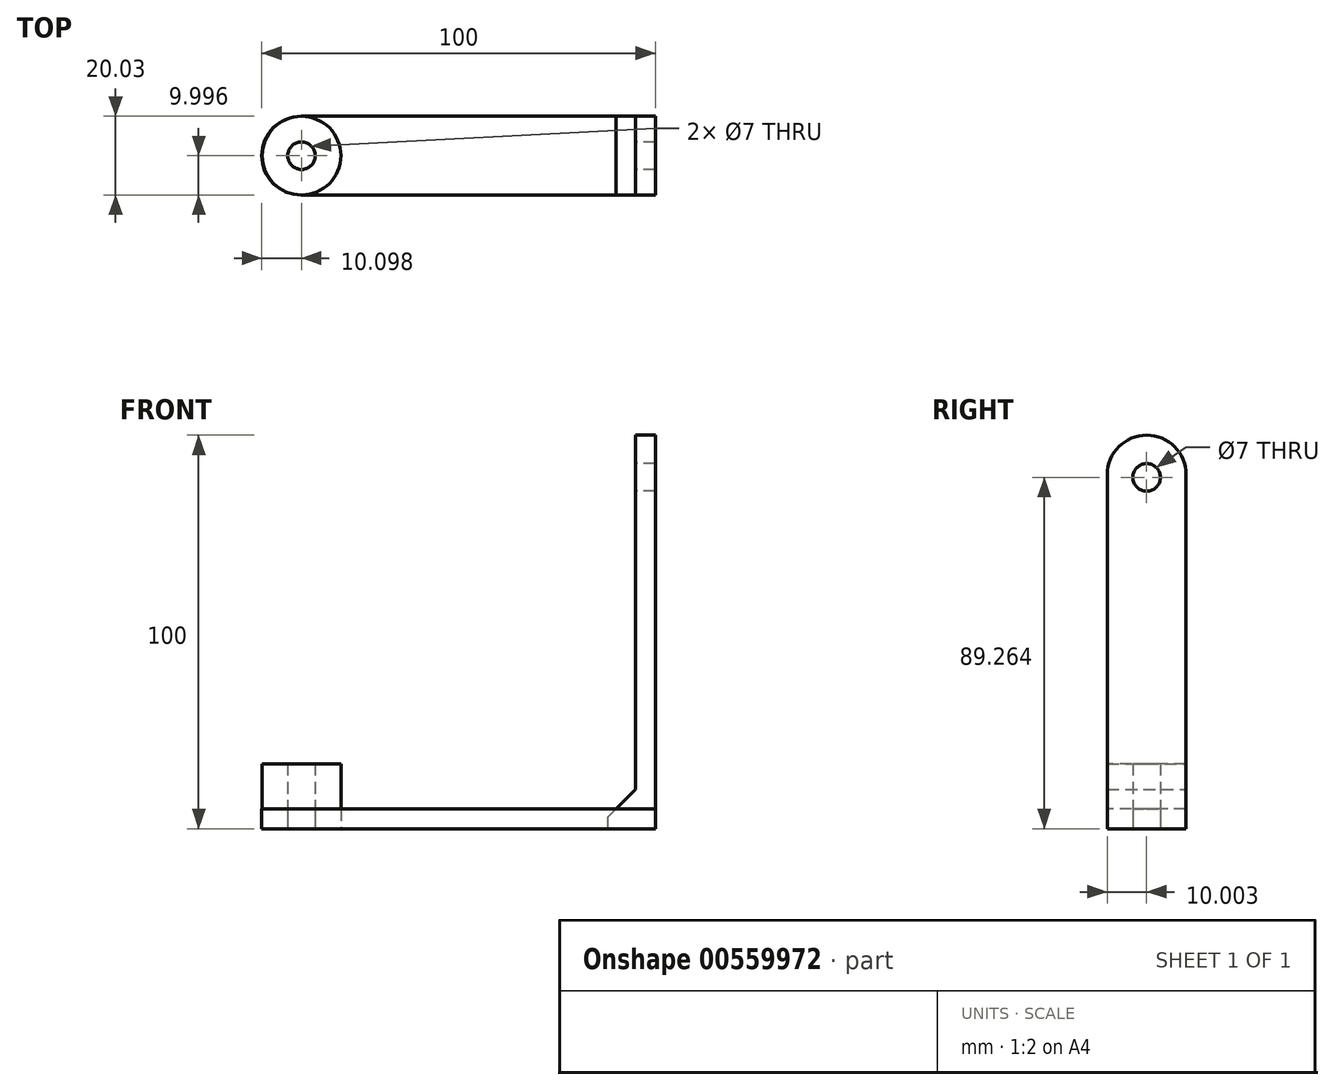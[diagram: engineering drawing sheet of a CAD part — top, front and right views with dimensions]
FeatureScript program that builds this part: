
annotation { "Feature Type Name" : "Feature", "Feature Type Description" : "" }
export const myFeature = defineFeature(function(context is Context, id is Id, definition is map)
    precondition{}
    {
        {
            var Q0;
            Q0=qCreatedBy(makeId("Top.planeOp"),FACE);
            var sketch = newSketch(context, id + "F0", { "sketchPlane" : qUnion([Q0])});
            skLineSegment(sketch, "E0.bottom", {"start": v(-46.2, 30.05) * mm, "end": v(53.8, 30.05) * mm});
            skLineSegment(sketch, "E0.top", {"start": v(-46.2, 10.05) * mm, "end": v(53.8, 10.05) * mm});
            skLineSegment(sketch, "E0.left", {"start": v(-46.2, 30.05) * mm, "end": v(-46.2, 10.05) * mm});
            skLineSegment(sketch, "E0.right", {"start": v(53.8, 30.05) * mm, "end": v(53.8, 10.05) * mm});
            skLineSegment(sketch, "E1", {"start": v(-46.2, 20.05) * mm, "end": v(53.8, 20.05) * mm, "construction": true});
            skCircle(sketch, "E2", {"center": v(-36.1, 20.05) * mm, "radius": 3.5 * mm});
            skCircle(sketch, "E3", {"center": v(-36.1, 20.05) * mm, "radius": 10 * mm});
            skSolve(sketch);
        }
        {
            var Q0;
            Q0=makeQuery(id+"F0.imprint","IMPRINT",FACE,{"disambiguationData":[TD([[makeQuery(id+"F0.imprint","IMPRINT",EDGE,{"derivedFrom":sQuery(id+"F0.wireOp",EDGE,"E0.bottom")}),-1.0]])]});
            var Q1;
            Q1=makeQuery(id+"F0.imprint","IMPRINT",FACE,{"disambiguationData":[TD([[makeQuery(id+"F0.imprint","IMPRINT",EDGE,{"derivedFrom":sQuery(id+"F0.wireOp",EDGE,"E2")}),-1.0]])]});
            extrude(context, id + "F1", {"entities" : qUnion([Q0, Q1]), "depth" : 5 * mm, "offsetDistance" : 25 * mm});
        }
        {
            var Q0;
            Q0=makeQuery(id+"F1.opExtrude","SWEPT_EDGE",EDGE,{"disambiguationData":[OSD([sQuery(id+"F0.wireOp",EDGE,"E0.bottom"),sQuery(id+"F0.wireOp",EDGE,"E0.left")])]});
            var Q1;
            Q1=makeQuery(id+"F1.opExtrude","SWEPT_EDGE",EDGE,{"disambiguationData":[OSD([sQuery(id+"F0.wireOp",EDGE,"E0.top"),sQuery(id+"F0.wireOp",EDGE,"E0.left")])]});
            fillet(context, id + "F2", {"entities" : qUnion([Q0, Q1]), "radius" : 10 * mm, "tangentPropagation" : true, "allowEdgeOverflow" : false});
        }
        {
            var Q0;
            Q0=qCreatedBy(makeId("Top.planeOp"),FACE);
            var sketch = newSketch(context, id + "F3", { "sketchPlane" : qUnion([Q0])});
            skLineSegment(sketch, "E4.bottom", {"start": v(53.8, 10.08) * mm, "end": v(48.8, 10.08) * mm});
            skLineSegment(sketch, "E4.top", {"start": v(53.8, 30.08) * mm, "end": v(48.8, 30.08) * mm});
            skLineSegment(sketch, "E4.left", {"start": v(53.8, 10.08) * mm, "end": v(53.8, 30.08) * mm});
            skLineSegment(sketch, "E4.right", {"start": v(48.8, 10.08) * mm, "end": v(48.8, 30.08) * mm});
            skLineSegment(sketch, "E5.bottom", {"start": v(48.8, 10.08) * mm, "end": v(41.8, 10.08) * mm});
            skLineSegment(sketch, "E5.top", {"start": v(48.8, 30.08) * mm, "end": v(41.8, 30.08) * mm});
            skLineSegment(sketch, "E5.right", {"start": v(41.8, 10.08) * mm, "end": v(41.8, 30.08) * mm});
            skSolve(sketch);
        }
        {
            var Q0;
            Q0=makeQuery(id+"F3.imprint","IMPRINT",FACE,{"disambiguationData":[TD([[makeQuery(id+"F3.imprint","IMPRINT",EDGE,{"derivedFrom":sQuery(id+"F3.wireOp",EDGE,"E4.bottom")}),-1.0]])]});
            extrude(context, id + "F4", {"entities" : qUnion([Q0]), "depth" : 100 * mm, "offsetDistance" : 25 * mm, "hasSecondDirection" : true, "secondDirectionOppositeDirection" : false, "secondDirectionDepth" : 5 * mm});
        }
        {
            var Q0;
            Q0=qCreatedBy(makeId("Right.planeOp"),FACE);
            var sketch = newSketch(context, id + "F5", { "sketchPlane" : qUnion([Q0])});
            skLineSegment(sketch, "E6", {"start": v(20.05, 99.76) * mm, "end": v(20.05, 0) * mm, "construction": true});
            skCircle(sketch, "E7", {"center": v(20.05, 89.26) * mm, "radius": 3.5 * mm});
            skSolve(sketch);
        }
        {
            var Q0;
            Q0=makeQuery(id+"F5.imprint","IMPRINT",FACE,{"disambiguationData":[TD([[makeQuery(id+"F5.imprint","IMPRINT",EDGE,{"derivedFrom":sQuery(id+"F5.wireOp",EDGE,"E7")}),1.0]])]});
            extrude(context, id + "F6", {"entities" : qUnion([Q0]), "operationType" : NewBodyOperationType.REMOVE, "depth" : 79.3 * mm, "offsetDistance" : 25 * mm});
        }
        {
            var Q0;
            Q0=makeQuery(id+"F4.opExtrude","CAP_EDGE",EDGE,{"disambiguationData":[OSD([sQuery(id+"F3.wireOp",EDGE,"E4.bottom")])],"isStart":false});
            var Q1;
            Q1=makeQuery(id+"F4.opExtrude","CAP_EDGE",EDGE,{"disambiguationData":[OSD([sQuery(id+"F3.wireOp",EDGE,"E4.top")])],"isStart":false});
            fillet(context, id + "F7", {"entities" : qUnion([Q0, Q1]), "radius" : 10 * mm, "tangentPropagation" : true, "allowEdgeOverflow" : false});
        }
        {
            var Q0;
            Q0=makeQuery(id+"F0.imprint","IMPRINT",FACE,{"disambiguationData":[TD([[makeQuery(id+"F0.imprint","IMPRINT",EDGE,{"derivedFrom":sQuery(id+"F0.wireOp",EDGE,"E2")}),-1.0]])]});
            extrude(context, id + "F8", {"entities" : qUnion([Q0]), "depth" : 16.5 * mm, "offsetDistance" : 25 * mm});
        }
        {
            var Q0;
            Q0=qSketchRegion(id+"F3",true);
            extrude(context, id + "F9", {"entities" : qUnion([Q0]), "operationType" : NewBodyOperationType.ADD, "depth" : 10 * mm, "offsetDistance" : 25 * mm});
        }
        {
            var Q0;
            Q0=makeQuery(id+"F9.opExtrude","CAP_EDGE",EDGE,{"disambiguationData":[OSD([sQuery(id+"F3.wireOp",EDGE,"E5.right")])],"isStart":false});
            chamfer(context, id + "F10", {"entities" : qUnion([Q0]), "width" : 7 * mm, "tangentPropagation" : true});
        }
    });
